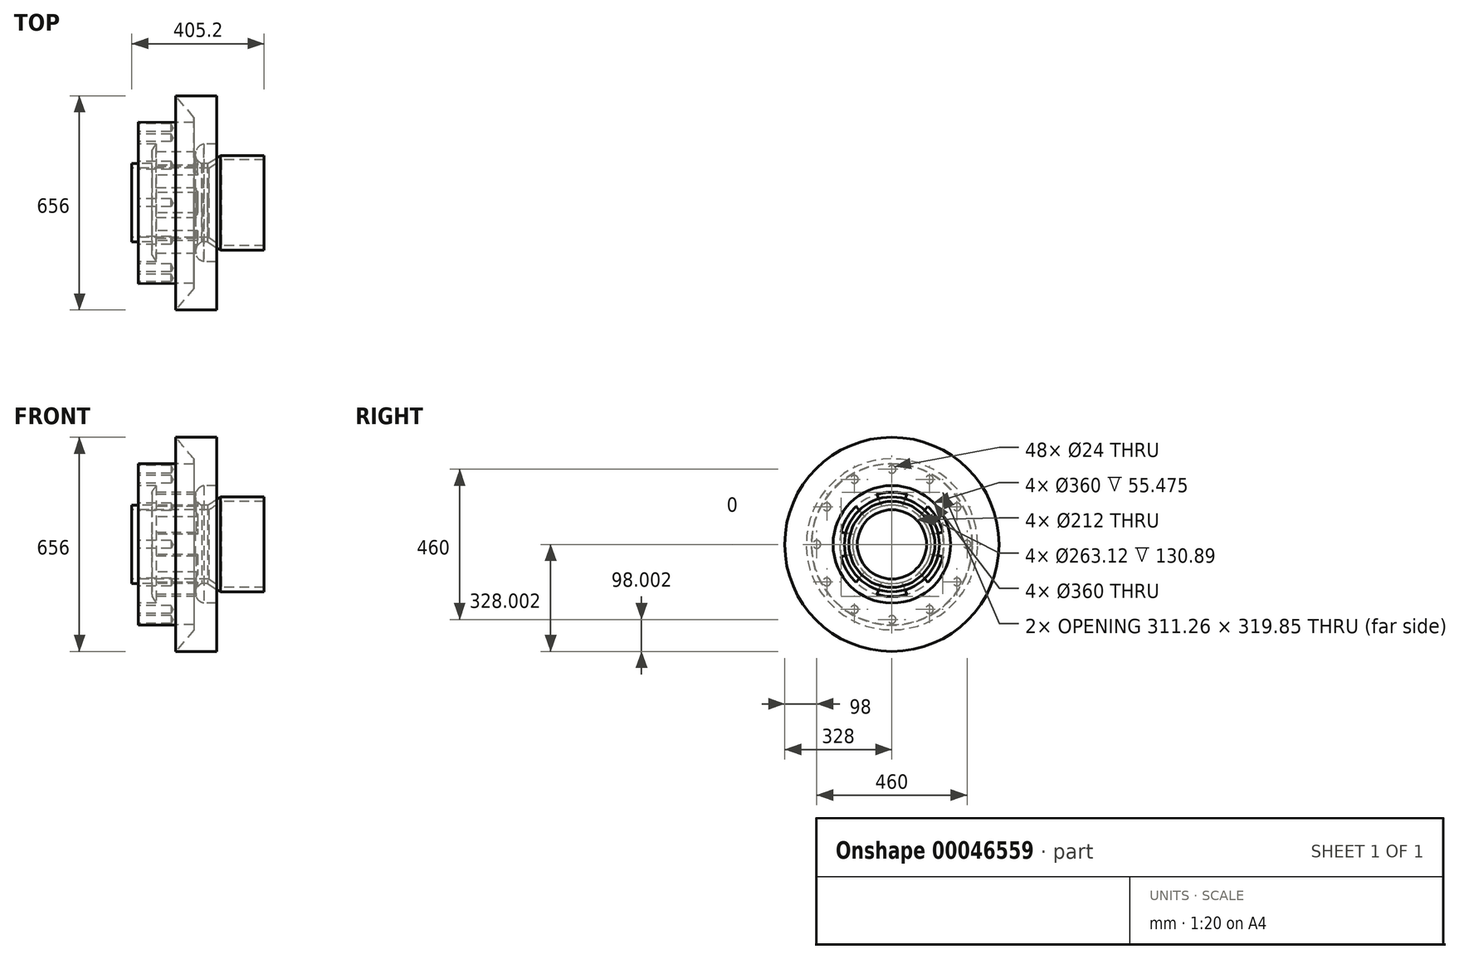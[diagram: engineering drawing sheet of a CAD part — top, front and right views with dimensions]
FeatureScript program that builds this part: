
annotation { "Feature Type Name" : "Feature", "Feature Type Description" : "" }
export const myFeature = defineFeature(function(context is Context, id is Id, definition is map)
    precondition{}
    {
        {
            var Q0;
            Q0=qCreatedBy(makeId("Front.planeOp"),FACE);
            var sketch = newSketch(context, id + "F0", { "sketchPlane" : qUnion([Q0])});
            skLineSegment(sketch, "E0", {"start": v(-1.64, 64.15) * mm, "end": v(-171.64, 65.51) * mm});
            skLineSegment(sketch, "E1", {"start": v(-171.64, 65.51) * mm, "end": v(-171.64, -1.85) * mm});
            skLineSegment(sketch, "E2", {"start": v(-171.64, -1.85) * mm, "end": v(-60.7, -1.85) * mm});
            skLineSegment(sketch, "E3.top", {"start": v(-60.7, -1.85) * mm, "end": v(68.36, -1.85) * mm});
            skLineSegment(sketch, "E4", {"start": v(-130.05, -21.85) * mm, "end": v(-116.17, -1.85) * mm});
            skLineSegment(sketch, "E5", {"start": v(-130.05, -21.85) * mm, "end": v(-130.05, -61.85) * mm});
            skLineSegment(sketch, "E6", {"start": v(-191.12, -75.85) * mm, "end": v(-191.26, -61.85) * mm});
            skLineSegment(sketch, "E7", {"start": v(-191.26, -61.85) * mm, "end": v(41.1, -61.85) * mm});
            skLineSegment(sketch, "E8", {"start": v(45.1, -75.85) * mm, "end": v(-191.12, -75.85) * mm});
            skArc(sketch, "E9", {"start": v(29.27, -1.85) * mm, "mid": v(3.92, -29.52) * mm, "end": v(22.98, -61.85) * mm});
            skLineSegment(sketch, "E10", {"start": v(41.1, -61.85) * mm, "end": v(80.45, -36.66) * mm});
            skLineSegment(sketch, "E11", {"start": v(80.45, -36.66) * mm, "end": v(213.94, -36.66) * mm});
            skLineSegment(sketch, "E12", {"start": v(213.94, -36.66) * mm, "end": v(213.94, -50.3) * mm});
            skLineSegment(sketch, "E13", {"start": v(213.94, -50.3) * mm, "end": v(83.05, -50.3) * mm});
            skLineSegment(sketch, "E3.right", {"start": v(68.36, 79.32) * mm, "end": v(68.36, -1.85) * mm});
            skLineSegment(sketch, "E14", {"start": v(68.36, 79.32) * mm, "end": v(68.36, 146.15) * mm});
            skLineSegment(sketch, "E15", {"start": v(-56.72, 146.15) * mm, "end": v(68.36, 146.15) * mm});
            skLineSegment(sketch, "E16", {"start": v(-1.52, 80.15) * mm, "end": v(-56.72, 146.15) * mm});
            skLineSegment(sketch, "E17", {"start": v(-1.52, 80.15) * mm, "end": v(-1.64, 64.15) * mm});
            skLineSegment(sketch, "E18", {"start": v(-219.16, -181.85) * mm, "end": v(182.27, -181.85) * mm, "construction": true});
            skLineSegment(sketch, "E19", {"start": v(45.1, -75.85) * mm, "end": v(83.05, -50.3) * mm});
            skSolve(sketch);
        }
        {
            var Q0;
            Q0=qSketchRegion(id+"F0",true);
            var Q1;
            Q1=sQuery(id+"F0.wireOp",EDGE,"E18");
            revolve(context, id + "F1", {"entities" : qUnion([Q0]), "axis" : qUnion([Q1]), "revolveType" : RevolveType.FULL});
        }
        {
            var Q0;
            Q0=makeQuery(id+"F1.opRevolve","SWEPT_FACE",FACE,{"disambiguationData":[OSD([sQuery(id+"F0.wireOp",EDGE,"E5")])]});
            var sketch = newSketch(context, id + "F2", { "sketchPlane" : qUnion([Q0])});
            skArc(sketch, "E20", {"start": v(45.93, -28.66) * mm, "mid": v(0, -21.92) * mm, "end": v(-45.93, -28.66) * mm});
            skArc(sketch, "E21", {"start": v(31.16, -66.2) * mm, "mid": v(0, -62.07) * mm, "end": v(-31.16, -66.2) * mm});
            skLineSegment(sketch, "E22", {"start": v(-45.96, -28.6) * mm, "end": v(-31.16, -66.2) * mm});
            skLineSegment(sketch, "E23.MirrorCS", {"start": v(45.96, -28.6) * mm, "end": v(31.16, -66.2) * mm});
            skLineSegment(sketch, "E24.1.0", {"start": v(-155.7, -145.02) * mm, "end": v(-115.74, -151) * mm});
            skArc(sketch, "E24.1.1", {"start": v(-84.58, -97.03) * mm, "mid": v(-103.73, -121.96) * mm, "end": v(-115.74, -151) * mm});
            skLineSegment(sketch, "E24.1.2", {"start": v(-109.75, -65.42) * mm, "end": v(-84.58, -97.03) * mm});
            skArc(sketch, "E24.1.3", {"start": v(-109.7, -65.48) * mm, "mid": v(-138.5, -101.88) * mm, "end": v(-155.63, -145.03) * mm});
            skLineSegment(sketch, "E24.2.0", {"start": v(-109.75, -298.28) * mm, "end": v(-84.58, -266.66) * mm});
            skArc(sketch, "E24.2.1", {"start": v(-115.74, -212.7) * mm, "mid": v(-103.73, -241.74) * mm, "end": v(-84.58, -266.66) * mm});
            skLineSegment(sketch, "E24.2.2", {"start": v(-155.7, -218.68) * mm, "end": v(-115.74, -212.7) * mm});
            skArc(sketch, "E24.2.3", {"start": v(-155.63, -218.67) * mm, "mid": v(-138.5, -261.81) * mm, "end": v(-109.7, -298.22) * mm});
            skLineSegment(sketch, "E24.3.0", {"start": v(45.96, -335.1) * mm, "end": v(31.16, -297.5) * mm});
            skArc(sketch, "E24.3.1", {"start": v(-31.16, -297.5) * mm, "mid": v(0, -301.63) * mm, "end": v(31.16, -297.5) * mm});
            skLineSegment(sketch, "E24.3.2", {"start": v(-45.96, -335.1) * mm, "end": v(-31.16, -297.5) * mm});
            skArc(sketch, "E24.3.3", {"start": v(-45.93, -335.04) * mm, "mid": v(0, -341.78) * mm, "end": v(45.93, -335.04) * mm});
            skLineSegment(sketch, "E24.4.0", {"start": v(155.7, -218.68) * mm, "end": v(115.74, -212.7) * mm});
            skArc(sketch, "E24.4.1", {"start": v(84.58, -266.66) * mm, "mid": v(103.73, -241.74) * mm, "end": v(115.74, -212.7) * mm});
            skLineSegment(sketch, "E24.4.2", {"start": v(109.75, -298.28) * mm, "end": v(84.58, -266.66) * mm});
            skArc(sketch, "E24.4.3", {"start": v(109.7, -298.22) * mm, "mid": v(138.5, -261.81) * mm, "end": v(155.63, -218.67) * mm});
            skLineSegment(sketch, "E24.5.0", {"start": v(109.75, -65.42) * mm, "end": v(84.58, -97.03) * mm});
            skArc(sketch, "E24.5.1", {"start": v(115.74, -151) * mm, "mid": v(103.73, -121.96) * mm, "end": v(84.58, -97.03) * mm});
            skLineSegment(sketch, "E24.5.2", {"start": v(155.7, -145.02) * mm, "end": v(115.74, -151) * mm});
            skArc(sketch, "E24.5.3", {"start": v(155.63, -145.03) * mm, "mid": v(138.5, -101.88) * mm, "end": v(109.7, -65.48) * mm});
            skSolve(sketch);
        }
        {
            var Q0;
            {var subQ5=sQuery(id+"F2.wireOp",EDGE,"E20");Q0=makeQuery(id+"F2.imprint","IMPRINT",FACE,{"disambiguationData":[TD([[makeQuery(id+"F2.imprint","IMPRINT",EDGE,{"derivedFrom":subQ5}),1.0]])]});}
            var Q1;
            {var subQ5=sQuery(id+"F2.wireOp",EDGE,"E24.4.3");Q1=makeQuery(id+"F2.imprint","IMPRINT",FACE,{"disambiguationData":[TD([[makeQuery(id+"F2.imprint","IMPRINT",EDGE,{"derivedFrom":subQ5}),1.0]])]});}
            var Q2;
            {var subQ5=sQuery(id+"F2.wireOp",EDGE,"E24.5.3");Q2=makeQuery(id+"F2.imprint","IMPRINT",FACE,{"disambiguationData":[TD([[makeQuery(id+"F2.imprint","IMPRINT",EDGE,{"derivedFrom":subQ5}),1.0]])]});}
            var Q3;
            {var subQ5=sQuery(id+"F2.wireOp",EDGE,"E24.3.3");Q3=makeQuery(id+"F2.imprint","IMPRINT",FACE,{"disambiguationData":[TD([[makeQuery(id+"F2.imprint","IMPRINT",EDGE,{"derivedFrom":subQ5}),1.0]])]});}
            var Q4;
            {var subQ5=sQuery(id+"F2.wireOp",EDGE,"E24.2.3");Q4=makeQuery(id+"F2.imprint","IMPRINT",FACE,{"disambiguationData":[TD([[makeQuery(id+"F2.imprint","IMPRINT",EDGE,{"derivedFrom":subQ5}),1.0]])]});}
            var Q5;
            {var subQ5=sQuery(id+"F2.wireOp",EDGE,"E24.1.3");Q5=makeQuery(id+"F2.imprint","IMPRINT",FACE,{"disambiguationData":[TD([[makeQuery(id+"F2.imprint","IMPRINT",EDGE,{"derivedFrom":subQ5}),1.0]])]});}
            var Q6;
            Q6=makeQuery(id+"F1.opRevolve","SWEPT_FACE",FACE,{"disambiguationData":[OSD([sQuery(id+"F0.wireOp",EDGE,"E5")])]});
            extrude(context, id + "F3", {"entities" : qUnion([Q0, Q1, Q2, Q3, Q4, Q5]), "operationType" : NewBodyOperationType.REMOVE, "oppositeDirection" : true, "endBoundEntityFace" : qUnion([Q6]), "depth" : 140 * mm});
        }
        {
            var Q0;
            Q0=makeQuery(id+"F1.opRevolve","SWEPT_FACE",FACE,{"disambiguationData":[OSD([sQuery(id+"F0.wireOp",EDGE,"E1")])]});
            var sketch = newSketch(context, id + "F4", { "sketchPlane" : qUnion([Q0])});
            skCircle(sketch, "E25", {"center": v(0, -181.85) * mm, "radius": 230 * mm});
            skCircle(sketch, "E26", {"center": v(0, 48.15) * mm, "radius": 12 * mm});
            skCircle(sketch, "E27.1.0", {"center": v(-115, 17.34) * mm, "radius": 12 * mm});
            skCircle(sketch, "E27.2.0", {"center": v(-199.19, -66.85) * mm, "radius": 12 * mm});
            skCircle(sketch, "E27.3.0", {"center": v(-230, -181.85) * mm, "radius": 12 * mm});
            skCircle(sketch, "E27.4.0", {"center": v(-199.19, -296.85) * mm, "radius": 12 * mm});
            skCircle(sketch, "E27.5.0", {"center": v(-115, -381.03) * mm, "radius": 12 * mm});
            skCircle(sketch, "E27.6.0", {"center": v(0, -411.85) * mm, "radius": 12 * mm});
            skCircle(sketch, "E27.7.0", {"center": v(115, -381.03) * mm, "radius": 12 * mm});
            skCircle(sketch, "E27.8.0", {"center": v(199.19, -296.85) * mm, "radius": 12 * mm});
            skCircle(sketch, "E27.9.0", {"center": v(230, -181.85) * mm, "radius": 12 * mm});
            skCircle(sketch, "E27.10.0", {"center": v(199.19, -66.85) * mm, "radius": 12 * mm});
            skCircle(sketch, "E27.11.0", {"center": v(115, 17.34) * mm, "radius": 12 * mm});
            skSolve(sketch);
        }
        {
            var Q0;
            Q0=sQuery(id+"F4.wireOp",VERTEX,"E27.1.0.center");
            var Q1;
            Q1=sQuery(id+"F4.wireOp",VERTEX,"E26.center");
            var Q2;
            Q2=sQuery(id+"F4.wireOp",VERTEX,"E27.11.0.center");
            var Q3;
            Q3=sQuery(id+"F4.wireOp",VERTEX,"E27.10.0.center");
            var Q4;
            Q4=sQuery(id+"F4.wireOp",VERTEX,"E27.9.0.center");
            var Q5;
            Q5=sQuery(id+"F4.wireOp",VERTEX,"E27.2.0.center");
            var Q6;
            Q6=sQuery(id+"F4.wireOp",VERTEX,"E27.3.0.center");
            var Q7;
            Q7=sQuery(id+"F4.wireOp",VERTEX,"E27.4.0.center");
            var Q8;
            Q8=sQuery(id+"F4.wireOp",VERTEX,"E27.5.0.center");
            var Q9;
            Q9=sQuery(id+"F4.wireOp",VERTEX,"E27.6.0.center");
            var Q10;
            Q10=sQuery(id+"F4.wireOp",VERTEX,"E27.7.0.center");
            var Q11;
            Q11=sQuery(id+"F4.wireOp",VERTEX,"E27.8.0.center");
            var Q12;
            Q12=makeQuery(id+"F1.opRevolve","SWEPT_BODY",BODY,{"disambiguationData":[OSD([sQuery(id+"F0.wireOp",EDGE,"E0"),sQuery(id+"F0.wireOp",EDGE,"E1"),sQuery(id+"F0.wireOp",EDGE,"E2"),sQuery(id+"F0.wireOp",EDGE,"E3.top"),sQuery(id+"F0.wireOp",EDGE,"E4"),sQuery(id+"F0.wireOp",EDGE,"E5"),sQuery(id+"F0.wireOp",EDGE,"E6"),sQuery(id+"F0.wireOp",EDGE,"E7"),sQuery(id+"F0.wireOp",EDGE,"E8"),sQuery(id+"F0.wireOp",EDGE,"E9"),sQuery(id+"F0.wireOp",EDGE,"E10"),sQuery(id+"F0.wireOp",EDGE,"E11"),sQuery(id+"F0.wireOp",EDGE,"E12"),sQuery(id+"F0.wireOp",EDGE,"E13"),sQuery(id+"F0.wireOp",EDGE,"8bd7945c-e339-46c6-a354-48875e3c8569"),sQuery(id+"F0.wireOp",EDGE,"E3.right"),sQuery(id+"F0.wireOp",EDGE,"E14"),sQuery(id+"F0.wireOp",EDGE,"E15"),sQuery(id+"F0.wireOp",EDGE,"E16"),sQuery(id+"F0.wireOp",EDGE,"E17")])]});
            hole(context, id + "F5", {"style" : HoleStyle.SIMPLE, "holeDiameter" : 24 * mm, "endStyle" : HoleEndStyle.BLIND, "holeDepth" : 100 * mm, "locations" : qUnion([Q0, Q1, Q2, Q3, Q4, Q5, Q6, Q7, Q8, Q9, Q10, Q11]), "scope" : qUnion([Q12])});
        }
    });
